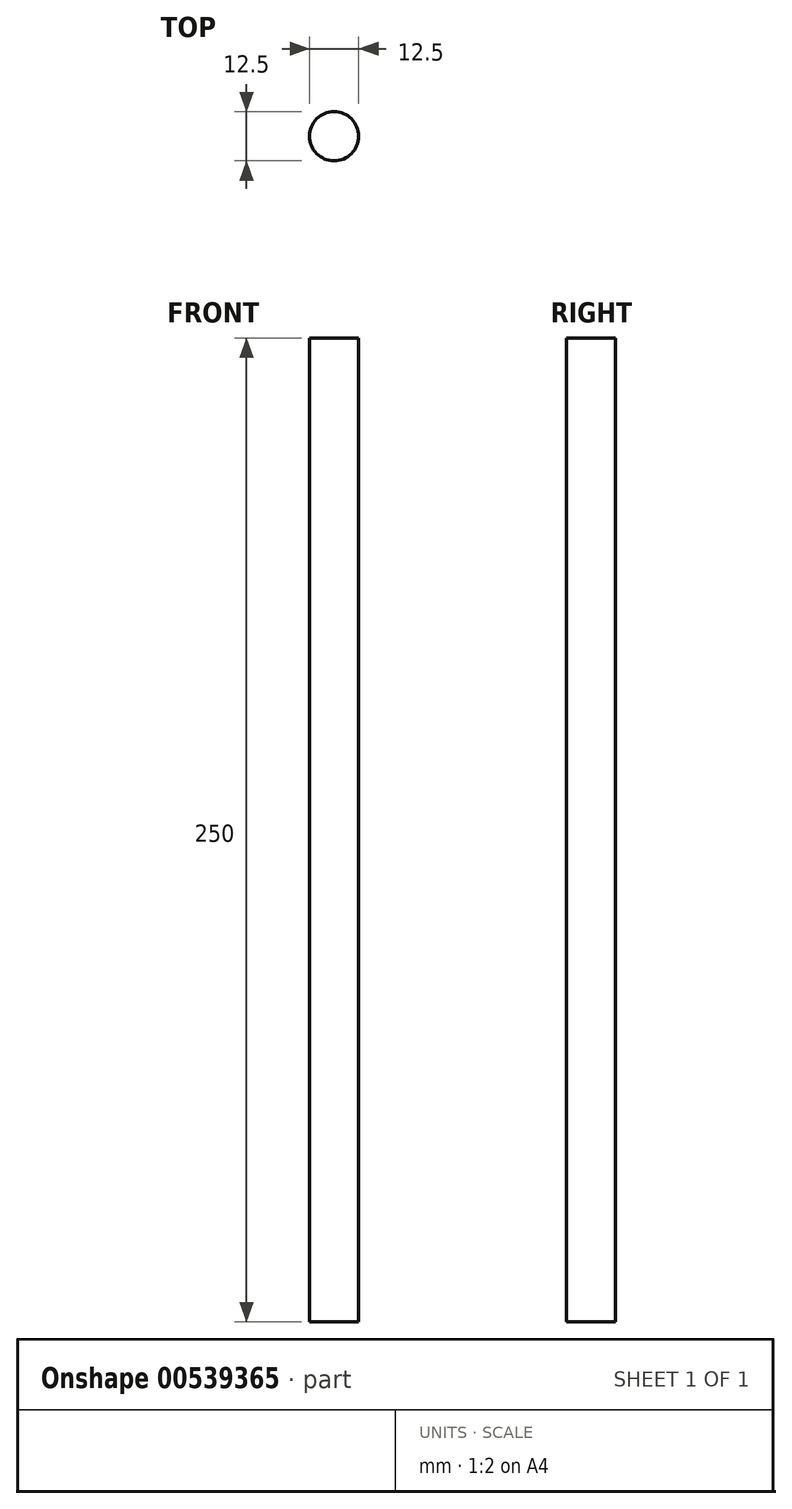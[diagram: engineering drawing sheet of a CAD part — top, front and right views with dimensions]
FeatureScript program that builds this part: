
annotation { "Feature Type Name" : "Feature", "Feature Type Description" : "" }
export const myFeature = defineFeature(function(context is Context, id is Id, definition is map)
    precondition{}
    {
        {
            var Q0;
            Q0=qCreatedBy(makeId("Top.planeOp"),FACE);
            var sketch = newSketch(context, id + "F0", { "sketchPlane" : qUnion([Q0])});
            skCircle(sketch, "E0", {"center": v(0, 0) * mm, "radius": 6.25 * mm});
            skSolve(sketch);
        }
        {
            var Q0;
            Q0 = qSketchRegion(id + "F0", true);
            extrude(context, id + "F1", {"entities" : qUnion([Q0]), "depth" : 250 * mm, "offsetDistance" : 25 * mm});
        }
    });
